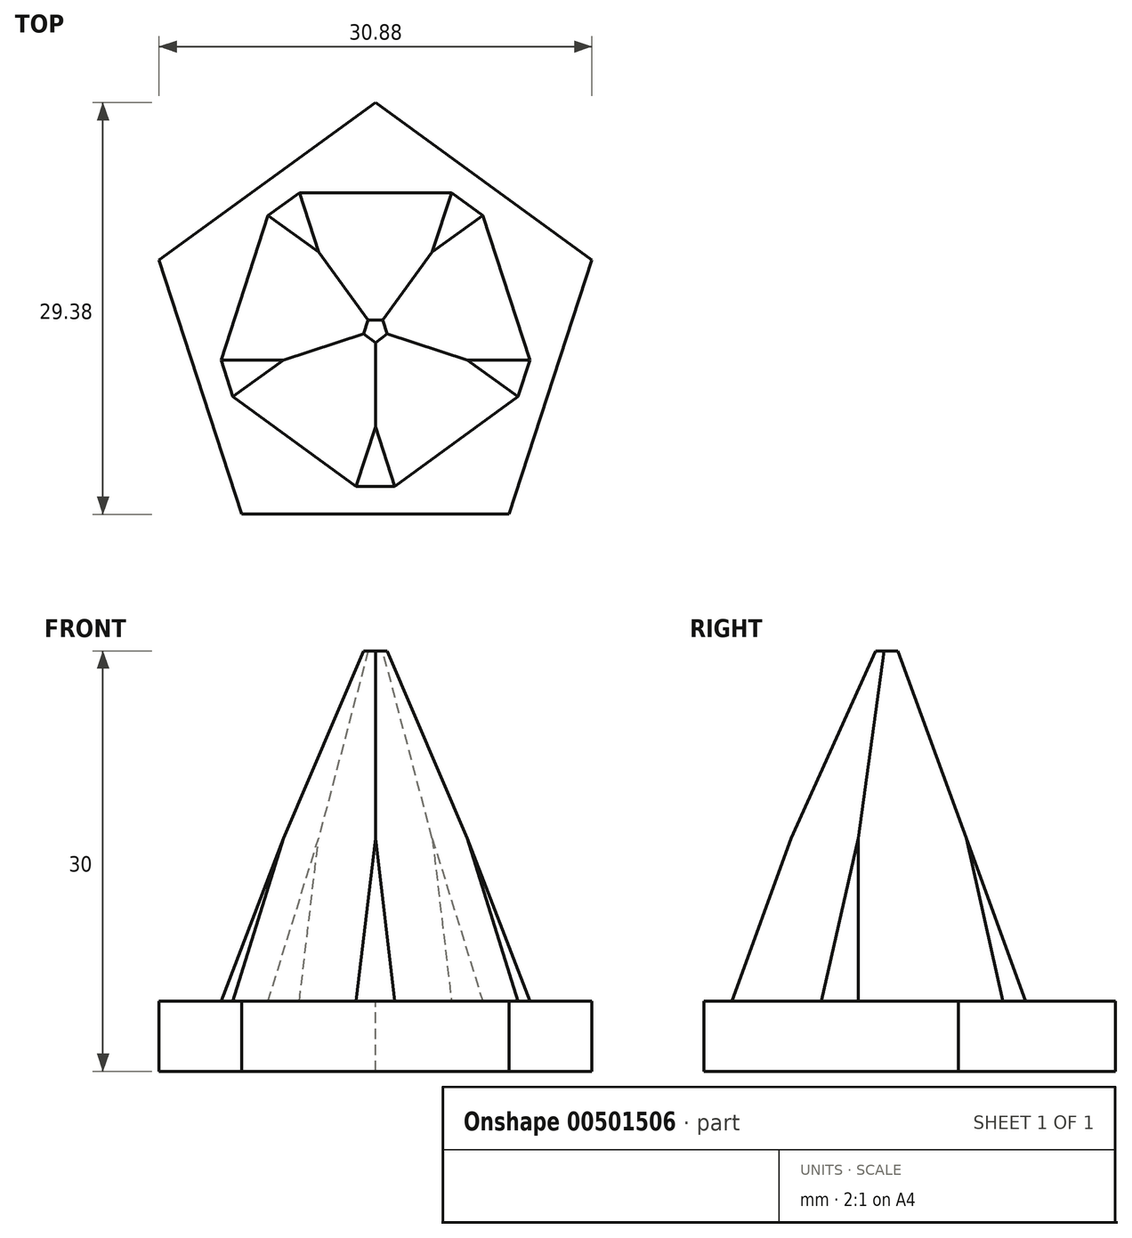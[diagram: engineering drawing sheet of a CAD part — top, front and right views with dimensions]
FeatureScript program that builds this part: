
annotation { "Feature Type Name" : "Feature", "Feature Type Description" : "" }
export const myFeature = defineFeature(function(context is Context, id is Id, definition is map)
    precondition{}
    {
        {
            var Q0;
            Q0=qCreatedBy(makeId("Top.planeOp"),FACE);
            var sketch = newSketch(context, id + "F0", { "sketchPlane" : qUnion([Q0])});
            skCircle(sketch, "E0.cCircle", {"center": v(0, 0) * mm, "radius": 15 * mm, "construction": true});
            skLineSegment(sketch, "E0.0", {"start": v(0, 15) * mm, "end": v(14.27, 4.64) * mm});
            skLineSegment(sketch, "E0.1", {"start": v(14.27, 4.64) * mm, "end": v(8.82, -12.14) * mm});
            skLineSegment(sketch, "E0.2", {"start": v(8.82, -12.14) * mm, "end": v(-8.82, -12.14) * mm});
            skLineSegment(sketch, "E0.3", {"start": v(-8.82, -12.14) * mm, "end": v(-14.27, 4.64) * mm});
            skLineSegment(sketch, "E0.4", {"start": v(-14.27, 4.64) * mm, "end": v(0, 15) * mm});
            skLineSegment(sketch, "E1.0", {"start": v(0, 16.24) * mm, "end": v(15.44, 5.02) * mm});
            skLineSegment(sketch, "E1.1", {"start": v(-15.44, 5.02) * mm, "end": v(0, 16.24) * mm});
            skLineSegment(sketch, "E1.2", {"start": v(15.44, 5.02) * mm, "end": v(9.54, -13.14) * mm});
            skLineSegment(sketch, "E1.3", {"start": v(9.54, -13.14) * mm, "end": v(-9.54, -13.14) * mm});
            skLineSegment(sketch, "E1.4", {"start": v(-9.54, -13.14) * mm, "end": v(-15.44, 5.02) * mm});
            skSolve(sketch);
        }
        {
            var Q0;
            Q0=qCreatedBy(makeId("Top.planeOp"),FACE);
            var sketch = newSketch(context, id + "F1", { "sketchPlane" : qUnion([Q0])});
            skCircle(sketch, "E2.0", {"center": v(0, 0) * mm, "radius": 15 * mm, "construction": true});
            skLineSegment(sketch, "E3.0", {"start": v(0, 15) * mm, "end": v(14.27, 4.64) * mm, "construction": true});
            skLineSegment(sketch, "E3.1", {"start": v(14.27, 4.64) * mm, "end": v(8.82, -12.14) * mm, "construction": true});
            skLineSegment(sketch, "E3.2", {"start": v(8.82, -12.14) * mm, "end": v(-8.82, -12.14) * mm, "construction": true});
            skLineSegment(sketch, "E3.3", {"start": v(-8.82, -12.14) * mm, "end": v(-14.27, 4.64) * mm, "construction": true});
            skLineSegment(sketch, "E3.4", {"start": v(-14.27, 4.64) * mm, "end": v(0, 15) * mm, "construction": true});
            skCircle(sketch, "E4.cCircle", {"center": v(0, 0) * mm, "radius": 12.14 * mm, "construction": true});
            skLineSegment(sketch, "E4.0", {"start": v(-1.38, -11.14) * mm, "end": v(-10.16, -4.75) * mm});
            skLineSegment(sketch, "E4.1", {"start": v(-11.02, -2.13) * mm, "end": v(-7.66, 8.2) * mm});
            skLineSegment(sketch, "E4.2", {"start": v(-5.43, 9.82) * mm, "end": v(5.43, 9.82) * mm});
            skLineSegment(sketch, "E4.3", {"start": v(7.66, 8.2) * mm, "end": v(11.02, -2.13) * mm});
            skLineSegment(sketch, "E4.4", {"start": v(10.16, -4.75) * mm, "end": v(1.38, -11.14) * mm});
            skLineSegment(sketch, "E5.0", {"start": v(0, 13.76) * mm, "end": v(13.1, 4.25) * mm, "construction": true});
            skLineSegment(sketch, "E5.1", {"start": v(-13.1, 4.25) * mm, "end": v(0, 13.76) * mm, "construction": true});
            skLineSegment(sketch, "E5.2", {"start": v(13.1, 4.25) * mm, "end": v(8.1, -11.14) * mm, "construction": true});
            skLineSegment(sketch, "E5.3", {"start": v(8.1, -11.14) * mm, "end": v(-8.1, -11.14) * mm, "construction": true});
            skLineSegment(sketch, "E5.4", {"start": v(-8.1, -11.14) * mm, "end": v(-13.1, 4.25) * mm, "construction": true});
            skPoint(sketch, "E6.orphan", {"position": v(-7.13, 9.82) * mm});
            skPoint(sketch, "E7.orphan", {"position": v(7.13, 9.82) * mm});
            skPoint(sketch, "E8.orphan", {"position": v(11.54, -3.75) * mm});
            skPoint(sketch, "E9.orphan", {"position": v(0, -12.14) * mm});
            skPoint(sketch, "E10.orphan", {"position": v(-11.54, -3.75) * mm});
            skLineSegment(sketch, "E11", {"start": v(-5.43, 9.82) * mm, "end": v(-7.66, 8.2) * mm});
            skLineSegment(sketch, "E12", {"start": v(5.43, 9.82) * mm, "end": v(7.66, 8.2) * mm});
            skLineSegment(sketch, "E13", {"start": v(11.02, -2.13) * mm, "end": v(10.16, -4.75) * mm});
            skLineSegment(sketch, "E14", {"start": v(1.38, -11.14) * mm, "end": v(-1.38, -11.14) * mm});
            skLineSegment(sketch, "E15", {"start": v(-10.16, -4.75) * mm, "end": v(-11.02, -2.13) * mm});
            skSolve(sketch);
        }
        {
            var Q0;
            Q0=makeQuery(id+"F0.imprint","IMPRINT",FACE,{"disambiguationData":[TD([[makeQuery(id+"F0.imprint","IMPRINT",EDGE,{"derivedFrom":sQuery(id+"F0.wireOp",EDGE,"E0.0")}),1.0]])]});
            var Q1;
            Q1=makeQuery(id+"F0.imprint","IMPRINT",FACE,{"disambiguationData":[TD([[makeQuery(id+"F0.imprint","IMPRINT",EDGE,{"derivedFrom":sQuery(id+"F0.wireOp",EDGE,"E0.0")}),-1.0]])]});
            extrude(context, id + "F2", {"entities" : qUnion([Q0, Q1]), "oppositeDirection" : true, "depth" : 5 * mm});
        }
        {
            var Q0;
            Q0=makeQuery(id+"F1.imprint","IMPRINT",FACE,{"disambiguationData":[TD([[makeQuery(id+"F1.imprint","IMPRINT",EDGE,{"derivedFrom":sQuery(id+"F1.wireOp",EDGE,"E4.0")}),-1.0]])]});
            extrude(context, id + "F3", {"entities" : qUnion([Q0]), "operationType" : NewBodyOperationType.ADD, "depth" : 25 * mm, "hasDraft" : true, "draftAngle" : 20 * degree, "draftPullDirection" : true});
        }
    });
